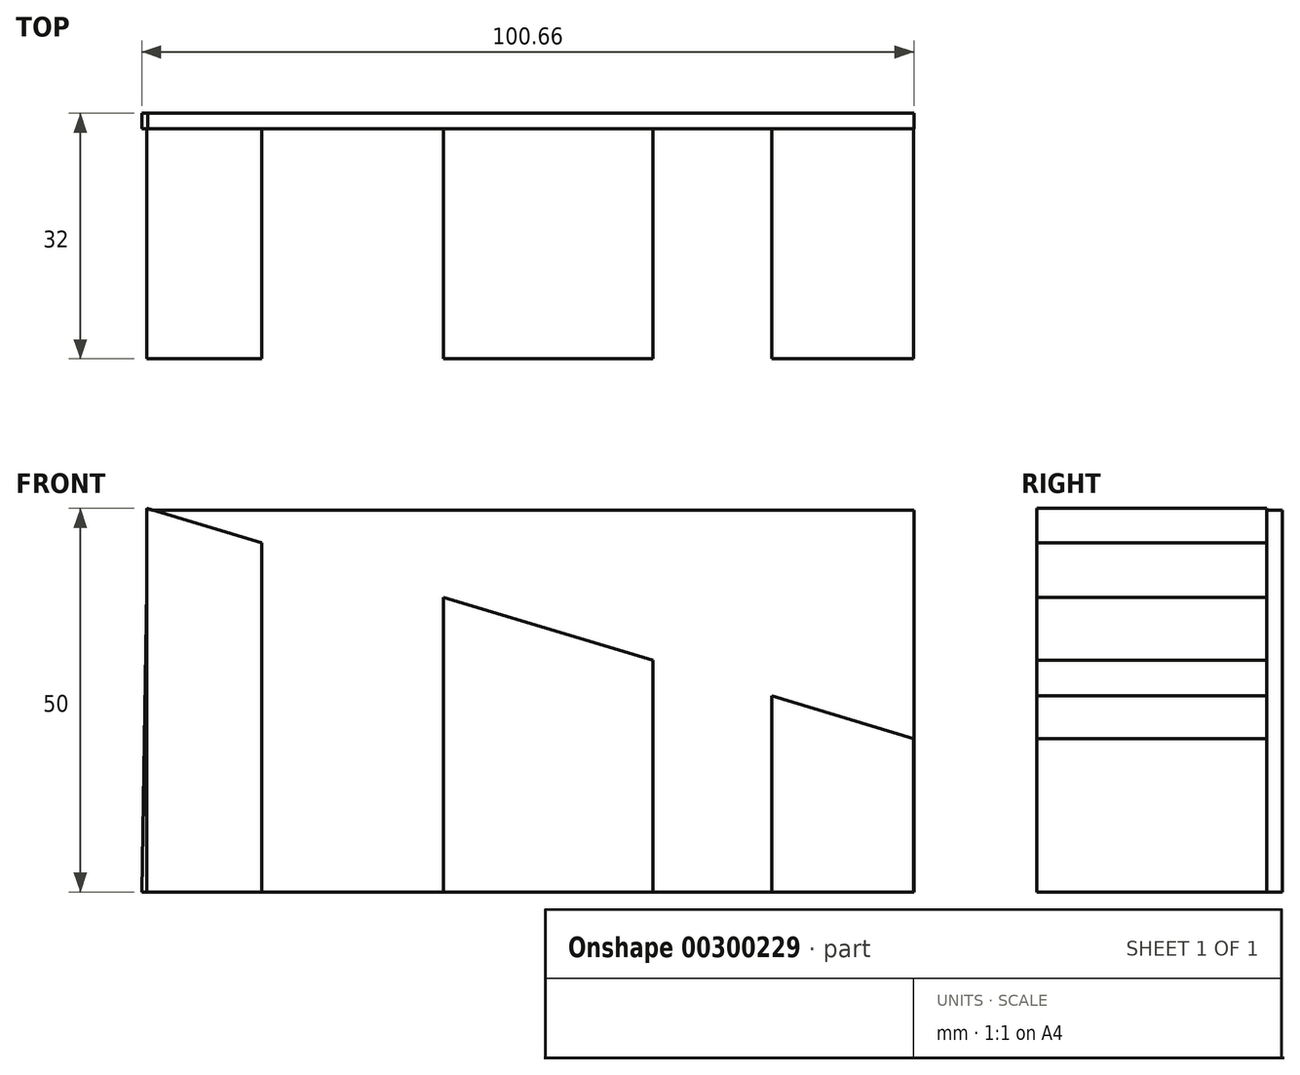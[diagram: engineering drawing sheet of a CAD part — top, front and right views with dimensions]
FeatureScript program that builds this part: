
annotation { "Feature Type Name" : "Feature", "Feature Type Description" : "" }
export const myFeature = defineFeature(function(context is Context, id is Id, definition is map)
    precondition{}
    {
        {
            var Q0;
            Q0=qCreatedBy(makeId("Front.planeOp"),FACE);
            var sketch = newSketch(context, id + "F0", { "sketchPlane" : qUnion([Q0])});
            skLineSegment(sketch, "E0", {"start": v(-81.5, 0) * mm, "end": v(-81.5, 50) * mm});
            skLineSegment(sketch, "E1", {"start": v(18.5, 20) * mm, "end": v(18.5, 0) * mm});
            skLineSegment(sketch, "E2", {"start": v(18.5, 0) * mm, "end": v(-81.5, 0) * mm});
            skLineSegment(sketch, "E3", {"start": v(-81.5, 50) * mm, "end": v(18.5, 20) * mm});
            skLineSegment(sketch, "E4", {"start": v(-66.65, 45.54) * mm, "end": v(-66.65, 0) * mm});
            skLineSegment(sketch, "E5", {"start": v(-42.84, 0) * mm, "end": v(-42.84, 38.4) * mm});
            skLineSegment(sketch, "E6", {"start": v(-15.49, 0) * mm, "end": v(-15.49, 30.2) * mm});
            skSolve(sketch);
        }
        {
            var Q0;
            {var subQ0=sQuery(id+"F0.wireOp",EDGE,"E5");Q0=makeQuery(id+"F0.imprint","IMPRINT",FACE,{"disambiguationData":[TD([[makeQuery(id+"F0.imprint","IMPRINT",EDGE,{"derivedFrom":subQ0}),-1.0]])]});}
            var Q1;
            {var subQ0=sQuery(id+"F0.wireOp",EDGE,"E4");Q1=makeQuery(id+"F0.imprint","IMPRINT",FACE,{"disambiguationData":[TD([[makeQuery(id+"F0.imprint","IMPRINT",EDGE,{"derivedFrom":subQ0}),1.0]])]});}
            var Q2;
            {var subQ0=sQuery(id+"F0.wireOp",EDGE,"E0");Q2=makeQuery(id+"F0.imprint","IMPRINT",FACE,{"disambiguationData":[TD([[makeQuery(id+"F0.imprint","IMPRINT",EDGE,{"derivedFrom":subQ0}),-1.0]])]});}
            var Q3;
            {var subQ0=sQuery(id+"F0.wireOp",EDGE,"E1");Q3=makeQuery(id+"F0.imprint","IMPRINT",FACE,{"disambiguationData":[TD([[makeQuery(id+"F0.imprint","IMPRINT",EDGE,{"derivedFrom":subQ0}),-1.0]])]});}
            extrude(context, id + "F1", {"entities" : qUnion([Q0, Q1, Q2, Q3]), "depth" : 30 * mm});
        }
        {
            var Q0;
            Q0=makeQuery(id+"F1.opExtrude","CAP_FACE",FACE,{"disambiguationData":[OSD([sQuery(id+"F0.wireOp",EDGE,"E0"),sQuery(id+"F0.wireOp",EDGE,"E1"),sQuery(id+"F0.wireOp",EDGE,"E2"),sQuery(id+"F0.wireOp",EDGE,"E3")])],"isStart":false});
            var sketch = newSketch(context, id + "F2", { "sketchPlane" : qUnion([Q0])});
            skLineSegment(sketch, "E7", {"start": v(-66.46, 0) * mm, "end": v(-66.46, 45.49) * mm});
            skLineSegment(sketch, "E8", {"start": v(-42.83, 0) * mm, "end": v(-42.83, 38.4) * mm});
            skLineSegment(sketch, "E9", {"start": v(-15.47, 0) * mm, "end": v(-15.47, 30.19) * mm});
            skLineSegment(sketch, "E10", {"start": v(0, 0) * mm, "end": v(0, 25.55) * mm});
            skSolve(sketch);
        }
        {
            var Q0;
            Q0 = qSketchRegion(id + "F2", true);
            var Q1;
            {var subQ0=sQuery(id+"F2.wireOp",EDGE,"E7");Q1=makeQuery(id+"F2.imprint","IMPRINT",FACE,{"disambiguationData":[TD([[makeQuery(id+"F2.imprint","IMPRINT",EDGE,{"derivedFrom":subQ0}),-1.0]])]});}
            var Q2;
            {var subQ0=sQuery(id+"F2.wireOp",EDGE,"E9");Q2=makeQuery(id+"F2.imprint","IMPRINT",FACE,{"disambiguationData":[TD([[makeQuery(id+"F2.imprint","IMPRINT",EDGE,{"derivedFrom":subQ0}),-1.0]])]});}
            extrude(context, id + "F3", {"entities" : qUnion([Q0, Q1, Q2]), "operationType" : NewBodyOperationType.REMOVE, "endBound" : BoundingType.THROUGH_ALL, "oppositeDirection" : true, "depth" : 25 * mm});
        }
        {
            var Q0;
            Q0=qCreatedBy(makeId("Front.planeOp"),FACE);
            var sketch = newSketch(context, id + "F4", { "sketchPlane" : qUnion([Q0])});
            skLineSegment(sketch, "E11", {"start": v(-81.34, 49.8) * mm, "end": v(18.53, 20.32) * mm});
            skLineSegment(sketch, "E12", {"start": v(18.53, 20.32) * mm, "end": v(18.53, 0) * mm});
            skLineSegment(sketch, "E13", {"start": v(18.53, 0) * mm, "end": v(0, 0) * mm});
            skLineSegment(sketch, "E14", {"start": v(0, 0) * mm, "end": v(-82.13, 0) * mm});
            skLineSegment(sketch, "E15", {"start": v(-82.13, 0) * mm, "end": v(-81.34, 49.8) * mm});
            skLineSegment(sketch, "E16.bottom", {"start": v(-81.34, 49.8) * mm, "end": v(18.53, 49.8) * mm});
            skLineSegment(sketch, "E16.top", {"start": v(-81.34, 0) * mm, "end": v(18.53, 0) * mm});
            skLineSegment(sketch, "E16.left", {"start": v(-81.34, 49.8) * mm, "end": v(-81.34, 0) * mm});
            skLineSegment(sketch, "E16.right", {"start": v(18.53, 49.8) * mm, "end": v(18.53, 0) * mm});
            skSolve(sketch);
        }
        {
            var Q0;
            Q0 = qSketchRegion(id + "F4", true);
            extrude(context, id + "F5", {"entities" : qUnion([Q0]), "operationType" : NewBodyOperationType.ADD, "oppositeDirection" : true, "depth" : 2 * mm});
        }
    });
